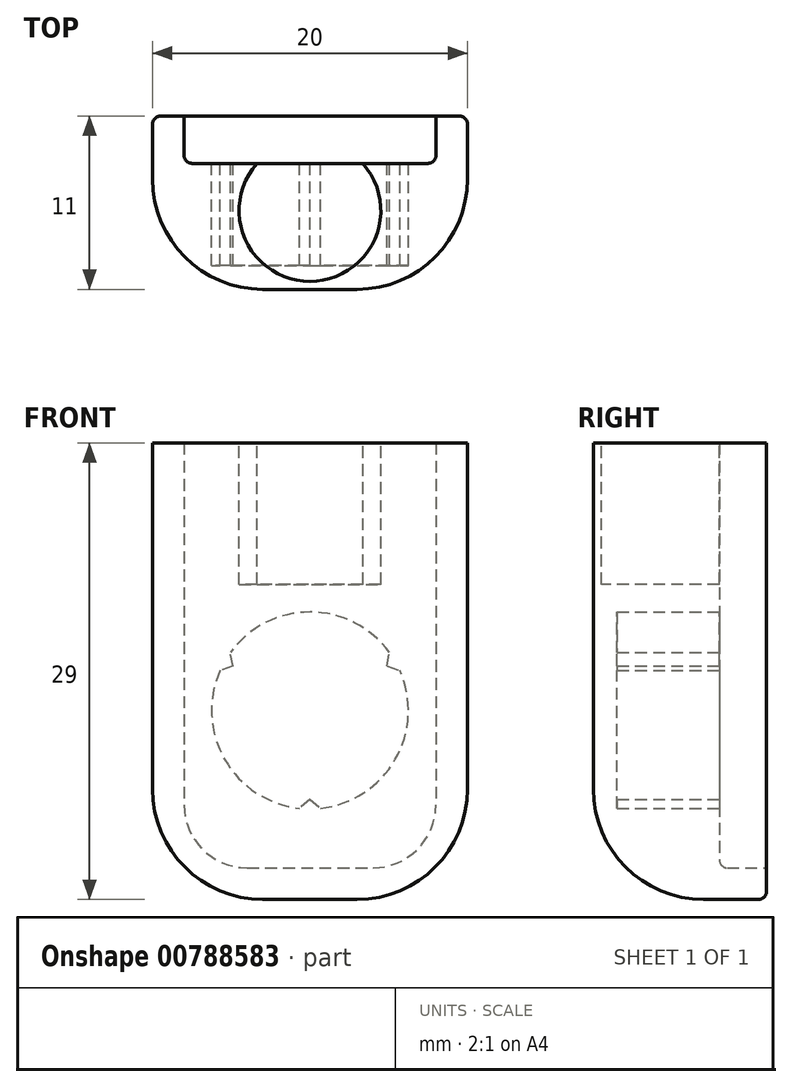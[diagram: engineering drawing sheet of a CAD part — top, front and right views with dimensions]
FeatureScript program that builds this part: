
annotation { "Feature Type Name" : "Feature", "Feature Type Description" : "" }
export const myFeature = defineFeature(function(context is Context, id is Id, definition is map)
    precondition{}
    {
        {
            var Q0;
            Q0=qCreatedBy(makeId("Front.planeOp"),FACE);
            var sketch = newSketch(context, id + "F0", { "sketchPlane" : qUnion([Q0])});
            skLineSegment(sketch, "E0.bottom", {"start": v(10, -14.5) * mm, "end": v(-10, -14.5) * mm});
            skLineSegment(sketch, "E0.top", {"start": v(10, 14.5) * mm, "end": v(-10, 14.5) * mm});
            skLineSegment(sketch, "E0.left", {"start": v(10, -14.5) * mm, "end": v(10, 14.5) * mm});
            skLineSegment(sketch, "E0.right", {"start": v(-10, -14.5) * mm, "end": v(-10, 14.5) * mm});
            skPoint(sketch, "E0.middle", {"position": v(0, 0) * mm});
            skSolve(sketch);
        }
        {
            var Q0;
            Q0 = qSketchRegion(id + "F0", true);
            extrude(context, id + "F1", {"entities" : qUnion([Q0]), "depth" : 11 * mm, "offsetDistance" : 25 * mm});
        }
        {
            var Q0;
            Q0=makeQuery(id+"F0.imprint","IMPRINT",FACE,{"disambiguationData":[TD([[makeQuery(id+"F0.imprint","IMPRINT",EDGE,{"derivedFrom":sQuery(id+"F0.wireOp",EDGE,"E0.bottom")}),-1.0]])]});
            var sketch = newSketch(context, id + "F2", { "sketchPlane" : qUnion([Q0])});
            skLineSegment(sketch, "E1.bottom", {"start": v(-8, 17.5) * mm, "end": v(8, 17.5) * mm});
            skLineSegment(sketch, "E1.top", {"start": v(-8, -12.5) * mm, "end": v(8, -12.5) * mm});
            skLineSegment(sketch, "E1.left", {"start": v(-8, 17.5) * mm, "end": v(-8, -12.5) * mm});
            skLineSegment(sketch, "E1.right", {"start": v(8, 17.5) * mm, "end": v(8, -12.5) * mm});
            skSolve(sketch);
        }
        {
            var Q0;
            Q0 = qSketchRegion(id + "F2", true);
            extrude(context, id + "F3", {"entities" : qUnion([Q0]), "operationType" : NewBodyOperationType.REMOVE, "depth" : 3 * mm, "offsetDistance" : 25 * mm});
        }
        {
            var Q0;
            Q0=makeQuery(id+"F3.boolean.opBoolean","COPY",FACE,{"derivedFrom":makeQuery(id+"F3.opExtrude","CAP_FACE",FACE,{"disambiguationData":[OSD([sQuery(id+"F2.wireOp",EDGE,"E1.bottom"),sQuery(id+"F2.wireOp",EDGE,"E1.top"),sQuery(id+"F2.wireOp",EDGE,"E1.left"),sQuery(id+"F2.wireOp",EDGE,"E1.right")])],"isStart":false})});
            var sketch = newSketch(context, id + "F4", { "sketchPlane" : qUnion([Q0])});
            skLineSegment(sketch, "E2", {"start": v(0, -12.5) * mm, "end": v(0, -2.5) * mm, "construction": true});
            skArc(sketch, "E3", {"start": v(0.66, -8.72) * mm, "mid": v(5.41, -5.63) * mm, "end": v(5.71, 0.04) * mm});
            skLineSegment(sketch, "E4", {"start": v(0, -8.75) * mm, "end": v(0, -8.15) * mm, "construction": true});
            skLineSegment(sketch, "E5", {"start": v(0, -8.15) * mm, "end": v(-0.66, -8.72) * mm});
            skLineSegment(sketch, "E6.MirrorCS", {"start": v(0, -8.15) * mm, "end": v(0.66, -8.72) * mm});
            skLineSegment(sketch, "E7.1.0", {"start": v(4.9, 0.32) * mm, "end": v(5.71, 0.04) * mm});
            skLineSegment(sketch, "E7.1.1", {"start": v(4.9, 0.32) * mm, "end": v(5.05, 1.18) * mm});
            skLineSegment(sketch, "E7.2.0", {"start": v(-4.9, 0.32) * mm, "end": v(-5.05, 1.18) * mm});
            skLineSegment(sketch, "E7.2.1", {"start": v(-4.9, 0.32) * mm, "end": v(-5.71, 0.04) * mm});
            skArc(sketch, "E8.trimOffspring", {"start": v(5.05, 1.18) * mm, "mid": v(0, 3.75) * mm, "end": v(-5.05, 1.18) * mm});
            skArc(sketch, "E9.trimOffspring", {"start": v(-5.71, 0.04) * mm, "mid": v(-5.24, -5.9) * mm, "end": v(0, -8.75) * mm});
            skSolve(sketch);
        }
        {
            var Q0;
            Q0 = qSketchRegion(id + "F4", true);
            extrude(context, id + "F5", {"entities" : qUnion([Q0]), "operationType" : NewBodyOperationType.REMOVE, "oppositeDirection" : true, "depth" : 6.5 * mm, "offsetDistance" : 25 * mm});
        }
        {
            var Q0;
            Q0=makeQuery(id+"F1.opExtrude","SWEPT_FACE",FACE,{"disambiguationData":[OSD([sQuery(id+"F0.wireOp",EDGE,"E0.top")])]});
            var sketch = newSketch(context, id + "F6", { "sketchPlane" : qUnion([Q0])});
            skLineSegment(sketch, "E10", {"start": v(0, -11) * mm, "end": v(0, -6) * mm, "construction": true});
            skCircle(sketch, "E11", {"center": v(0, -6) * mm, "radius": 4.5 * mm});
            skSolve(sketch);
        }
        {
            var Q0;
            {var subQ0=sQuery(id+"F6.wireOp",EDGE,"E11");var subQ1=makeQuery(id+"F3.boolean.opBoolean","INTERSECT",EDGE,{"derivedFrom":[makeQuery(id+"F1.opExtrude","SWEPT_FACE",FACE,{"disambiguationData":[OSD([sQuery(id+"F0.wireOp",EDGE,"E0.top")])]}),makeQuery(id+"F3.opExtrude","CAP_FACE",FACE,{"disambiguationData":[OSD([sQuery(id+"F2.wireOp",EDGE,"E1.bottom"),sQuery(id+"F2.wireOp",EDGE,"E1.top"),sQuery(id+"F2.wireOp",EDGE,"E1.left"),sQuery(id+"F2.wireOp",EDGE,"E1.right")])],"isStart":false})]});var subQ2=makeQuery(id+"F6.imprint","INTERSECT",VERTEX,{"disambiguationData":[OD(0.0)],"derivedFrom":[subQ1,subQ0]});Q0=makeQuery(id+"F6.imprint","IMPRINT",FACE,{"disambiguationData":[TD([[makeQuery(id+"F6.imprint","IMPRINT",EDGE,{"disambiguationData":[TD([[subQ2,-1.0]])],"derivedFrom":subQ0}),1.0]])]});}
            extrude(context, id + "F7", {"entities" : qUnion([Q0]), "operationType" : NewBodyOperationType.REMOVE, "oppositeDirection" : true, "depth" : 9 * mm, "offsetDistance" : 25 * mm});
        }
        {
            var Q0;
            Q0=makeQuery(id+"F3.boolean.opBoolean","COPY",EDGE,{"derivedFrom":makeQuery(id+"F3.opExtrude","SWEPT_EDGE",EDGE,{"disambiguationData":[OSD([sQuery(id+"F2.wireOp",EDGE,"E1.top"),sQuery(id+"F2.wireOp",EDGE,"E1.right")])]})});
            var Q1;
            Q1=makeQuery(id+"F3.boolean.opBoolean","COPY",EDGE,{"derivedFrom":makeQuery(id+"F3.opExtrude","SWEPT_EDGE",EDGE,{"disambiguationData":[OSD([sQuery(id+"F2.wireOp",EDGE,"E1.top"),sQuery(id+"F2.wireOp",EDGE,"E1.left")])]})});
            fillet(context, id + "F8", {"entities" : qUnion([Q0, Q1]), "radius" : 4 * mm, "tangentPropagation" : true, "allowEdgeOverflow" : false});
        }
        {
            var Q0;
            Q0=makeQuery(id+"F1.opExtrude","SWEPT_EDGE",EDGE,{"disambiguationData":[OSD([sQuery(id+"F0.wireOp",EDGE,"E0.bottom"),sQuery(id+"F0.wireOp",EDGE,"E0.right")])]});
            var Q1;
            Q1=makeQuery(id+"F1.opExtrude","SWEPT_EDGE",EDGE,{"disambiguationData":[OSD([sQuery(id+"F0.wireOp",EDGE,"E0.bottom"),sQuery(id+"F0.wireOp",EDGE,"E0.left")])]});
            var Q2;
            Q2=makeQuery(id+"F1.opExtrude","CAP_EDGE",EDGE,{"disambiguationData":[OSD([sQuery(id+"F0.wireOp",EDGE,"E0.bottom")])],"isStart":false});
            var Q3;
            Q3=makeQuery(id+"F1.opExtrude","CAP_EDGE",EDGE,{"disambiguationData":[OSD([sQuery(id+"F0.wireOp",EDGE,"E0.left")])],"isStart":false});
            var Q4;
            Q4=makeQuery(id+"F1.opExtrude","CAP_EDGE",EDGE,{"disambiguationData":[OSD([sQuery(id+"F0.wireOp",EDGE,"E0.right")])],"isStart":false});
            fillet(context, id + "F9", {"entities" : qUnion([Q0, Q1, Q2, Q3, Q4]), "radius" : 7 * mm, "tangentPropagation" : true, "allowEdgeOverflow" : false});
        }
        {
            var Q0;
            Q0=makeQuery(id+"F3.boolean.opBoolean","COPY",EDGE,{"derivedFrom":makeQuery(id+"F3.opExtrude","CAP_EDGE",EDGE,{"disambiguationData":[OSD([sQuery(id+"F2.wireOp",EDGE,"E1.right")])],"isStart":false})});
            var Q1;
            Q1=makeQuery(id+"F1.opExtrude","CAP_EDGE",EDGE,{"disambiguationData":[OSD([sQuery(id+"F0.wireOp",EDGE,"E0.left")])],"isStart":true});
            fillet(context, id + "F10", {"entities" : qUnion([Q0, Q1]), "radius" : 0.5 * mm, "tangentPropagation" : true, "allowEdgeOverflow" : false});
        }
    });
